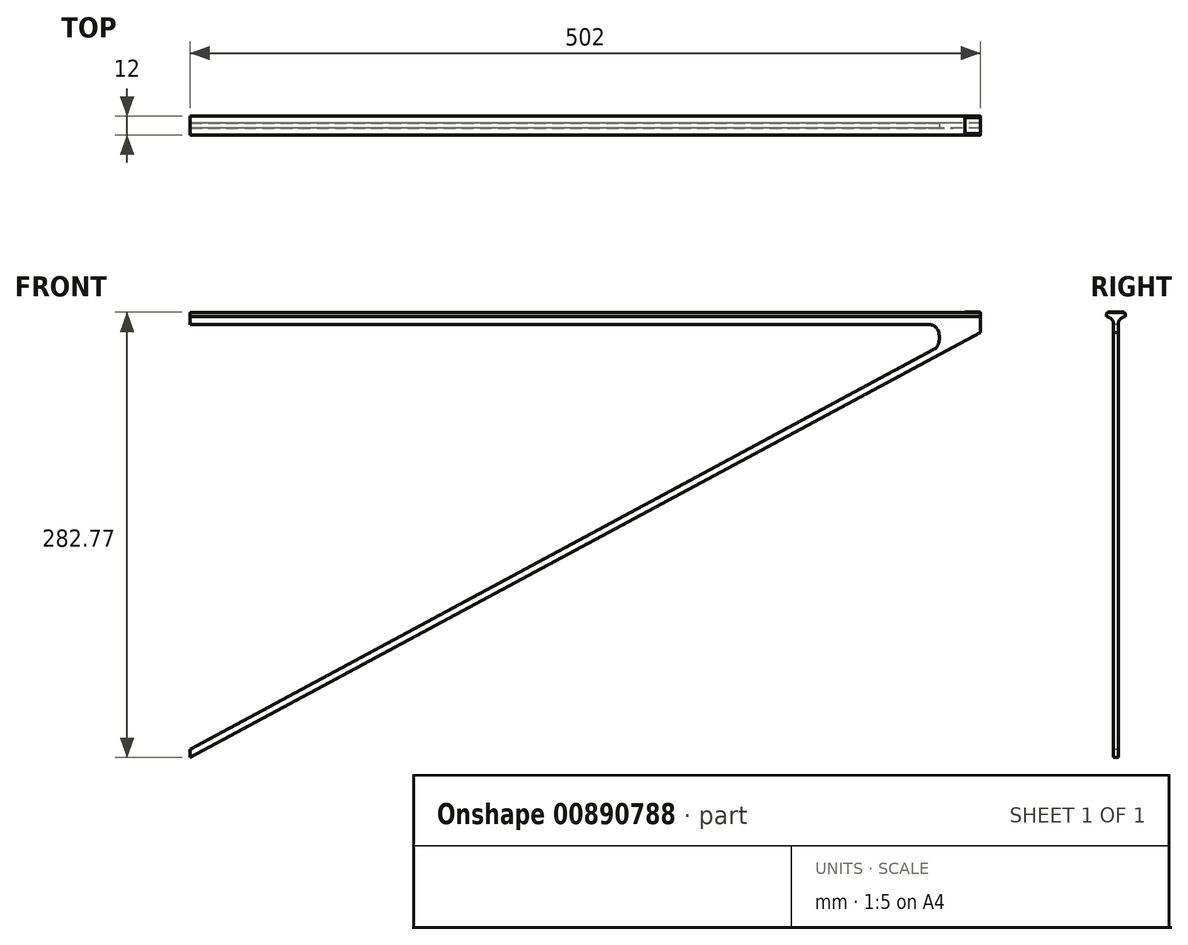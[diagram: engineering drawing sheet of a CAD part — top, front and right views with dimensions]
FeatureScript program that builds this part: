
annotation { "Feature Type Name" : "Feature", "Feature Type Description" : "" }
export const myFeature = defineFeature(function(context is Context, id is Id, definition is map)
    precondition{}
    {
        {
            var Q0;
            Q0=qCreatedBy(makeId("Right.planeOp"),FACE);
            var sketch = newSketch(context, id + "F0", { "sketchPlane" : qUnion([Q0])});
            skLineSegment(sketch, "E0", {"start": v(-6, 24.64) * mm, "end": v(6, 24.64) * mm});
            skLineSegment(sketch, "E1", {"start": v(-6, 24.64) * mm, "end": v(-6, 22.14) * mm});
            skLineSegment(sketch, "E2", {"start": v(-6, 22.14) * mm, "end": v(-1.5, 22.14) * mm});
            skLineSegment(sketch, "E3", {"start": v(-1.5, 22.14) * mm, "end": v(-1.5, -257.86) * mm});
            skLineSegment(sketch, "E4.MirrorCS", {"start": v(6, 22.14) * mm, "end": v(1.5, 22.14) * mm});
            skLineSegment(sketch, "E5.MirrorCS", {"start": v(6, 24.64) * mm, "end": v(6, 22.14) * mm});
            skLineSegment(sketch, "E6.MirrorCS", {"start": v(1.5, 22.14) * mm, "end": v(1.5, -257.86) * mm});
            skLineSegment(sketch, "E7", {"start": v(-1.5, -257.86) * mm, "end": v(1.5, -257.86) * mm});
            skSolve(sketch);
        }
        {
            var Q0;
            Q0=makeQuery(id+"F0.imprint","IMPRINT",FACE,{"disambiguationData":[TD([[makeQuery(id+"F0.imprint","IMPRINT",EDGE,{"derivedFrom":sQuery(id+"F0.wireOp",EDGE,"E0")}),-1.0]])]});
            extrude(context, id + "F1", {"entities" : qUnion([Q0]), "depth" : 502 * mm, "offsetDistance" : 25 * mm});
        }
        {
            var Q0;
            Q0=makeQuery(id+"F1.opExtrude","SWEPT_FACE",FACE,{"disambiguationData":[OSD([sQuery(id+"F0.wireOp",EDGE,"E3")])]});
            var sketch = newSketch(context, id + "F2", { "sketchPlane" : qUnion([Q0])});
            skPoint(sketch, "E8", {"position": v(502, 22.14) * mm});
            skPoint(sketch, "E9", {"position": v(502, 17.14) * mm});
            skPoint(sketch, "E10", {"position": v(0, -257.86) * mm});
            skPoint(sketch, "E11", {"position": v(0, -252.86) * mm});
            skLineSegment(sketch, "E12", {"start": v(502, 17.14) * mm, "end": v(0, 17.14) * mm});
            skLineSegment(sketch, "E13", {"start": v(502, 17.14) * mm, "end": v(0, -252.86) * mm});
            skPoint(sketch, "E14", {"position": v(502, 12.14) * mm});
            skLineSegment(sketch, "E15", {"start": v(0, -257.86) * mm, "end": v(502, 12.14) * mm});
            skSolve(sketch);
        }
        {
            var Q0;
            {var subQ0=sQuery(id+"F2.wireOp",EDGE,"E12");Q0=makeQuery(id+"F2.imprint","IMPRINT",FACE,{"disambiguationData":[TD([[makeQuery(id+"F2.imprint","IMPRINT",EDGE,{"derivedFrom":subQ0}),1.0]])]});}
            extrude(context, id + "F3", {"entities" : qUnion([Q0]), "operationType" : NewBodyOperationType.REMOVE, "oppositeDirection" : true, "depth" : 406 * mm, "offsetDistance" : 25 * mm});
        }
        {
            var Q0;
            {var subQ0=sQuery(id+"F2.wireOp",EDGE,"E15");Q0=makeQuery(id+"F2.imprint","IMPRINT",FACE,{"disambiguationData":[TD([[makeQuery(id+"F2.imprint","IMPRINT",EDGE,{"derivedFrom":subQ0}),-1.0]])]});}
            extrude(context, id + "F4", {"entities" : qUnion([Q0]), "operationType" : NewBodyOperationType.REMOVE, "oppositeDirection" : true, "depth" : 143 * mm, "offsetDistance" : 25 * mm});
        }
        {
            var Q0;
            Q0=makeQuery(id+"F3.boolean.opBoolean","COPY",FACE,{"derivedFrom":makeQuery(id+"F3.opExtrude","SWEPT_FACE",FACE,{"disambiguationData":[OSD([sQuery(id+"F2.wireOp",EDGE,"E12")])]})});
            var sketch = newSketch(context, id + "F5", { "sketchPlane" : qUnion([Q0])});
            skLineSegment(sketch, "E16.bottom", {"start": v(475.77, -1.5) * mm, "end": v(502, -1.5) * mm});
            skLineSegment(sketch, "E16.top", {"start": v(475.77, 1.5) * mm, "end": v(502, 1.5) * mm});
            skLineSegment(sketch, "E16.left", {"start": v(475.77, -1.5) * mm, "end": v(475.77, 1.5) * mm});
            skLineSegment(sketch, "E16.right", {"start": v(502, -1.5) * mm, "end": v(502, 1.5) * mm});
            skSolve(sketch);
        }
        {
            var Q0;
            Q0 = qSketchRegion(id + "F5", true);
            extrude(context, id + "F6", {"entities" : qUnion([Q0]), "operationType" : NewBodyOperationType.ADD, "depth" : 14.25 * mm, "offsetDistance" : 25 * mm, "hasSecondDirection" : true, "secondDirectionOppositeDirection" : true, "secondDirectionDepth" : 0.8 * mm});
        }
        {
            var Q0;
            {var subQ0=sQuery(id+"F0.wireOp",EDGE,"E7");var subQ1=sQuery(id+"F0.wireOp",EDGE,"E6.MirrorCS");var subQ3=sQuery(id+"F0.wireOp",EDGE,"E4.MirrorCS");var subQ10=makeQuery(id+"F1.opExtrude","SWEPT_FACE",FACE,{"disambiguationData":[OSD([subQ1])]});Q0=makeQuery(id+"F6.boolean.opBoolean","MERGE",FACE,{"derivedFrom":[makeQuery(id+"F3.boolean.opBoolean","SPLIT",FACE,{"disambiguationData":[TD([makeQuery(id+"F1.opExtrude","SWEPT_FACE",FACE,{"disambiguationData":[OSD([subQ3])]})])],"derivedFrom":subQ10}),makeQuery(id+"F3.boolean.opBoolean","SPLIT",FACE,{"disambiguationData":[TD([makeQuery(id+"F1.opExtrude","SWEPT_FACE",FACE,{"disambiguationData":[OSD([subQ0])]})])],"derivedFrom":subQ10}),makeQuery(id+"F6.opExtrude","SWEPT_FACE",FACE,{"disambiguationData":[OSD([sQuery(id+"F5.wireOp",EDGE,"E16.bottom")])]})]});}
            var sketch = newSketch(context, id + "F7", { "sketchPlane" : qUnion([Q0])});
            skLineSegment(sketch, "E17", {"start": v(-502, 12.14) * mm, "end": v(-484.8, 2.9) * mm});
            skLineSegment(sketch, "E18", {"start": v(-484.8, 2.9) * mm, "end": v(-502, 2.9) * mm});
            skLineSegment(sketch, "E19", {"start": v(-502, 2.9) * mm, "end": v(-502, 12.14) * mm});
            skSolve(sketch);
        }
        {
            var Q0;
            Q0=makeQuery(id+"F7.imprint","IMPRINT",FACE,{"disambiguationData":[TD([[makeQuery(id+"F7.imprint","IMPRINT",EDGE,{"derivedFrom":sQuery(id+"F7.wireOp",EDGE,"E17")}),-1.0]])]});
            extrude(context, id + "F8", {"entities" : qUnion([Q0]), "operationType" : NewBodyOperationType.REMOVE, "oppositeDirection" : true, "depth" : 25 * mm, "offsetDistance" : 25 * mm});
        }
        {
            var Q0;
            Q0=makeQuery(id+"F1.opExtrude","SWEPT_FACE",FACE,{"disambiguationData":[OSD([sQuery(id+"F0.wireOp",EDGE,"E0")])]});
            var sketch = newSketch(context, id + "F9", { "sketchPlane" : qUnion([Q0])});
            skLineSegment(sketch, "E20", {"start": v(496.5, -5.96) * mm, "end": v(496.5, -4.96) * mm});
            skLineSegment(sketch, "E21", {"start": v(497.84, 5.98) * mm, "end": v(497.84, 4.98) * mm});
            skLineSegment(sketch, "E22", {"start": v(501.98, 4.98) * mm, "end": v(491.98, 4.98) * mm});
            skLineSegment(sketch, "E23", {"start": v(491.98, 4.98) * mm, "end": v(491.98, -5.02) * mm});
            skLineSegment(sketch, "E24", {"start": v(491.98, -5.02) * mm, "end": v(501.98, -5.02) * mm});
            skLineSegment(sketch, "E25", {"start": v(501.98, -5.02) * mm, "end": v(501.98, 4.98) * mm});
            skSolve(sketch);
        }
        {
            var Q0;
            {var subQ6=sQuery(id+"F9.wireOp",EDGE,"oiYsljUy-fvYa-lGQO-kkHg-lW1iThUNzZ6y");Q0=makeQuery(id+"F9.imprint","IMPRINT",FACE,{"disambiguationData":[TD([[makeQuery(id+"F9.imprint","IMPRINT",EDGE,{"derivedFrom":subQ6}),1.0]])]});}
            var Q1;
            {var subQ1=sQuery(id+"F9.wireOp",EDGE,"E23");Q1=makeQuery(id+"F9.imprint","IMPRINT",FACE,{"disambiguationData":[TD([[makeQuery(id+"F9.imprint","IMPRINT",EDGE,{"derivedFrom":subQ1}),1.0]])]});}
            extrude(context, id + "F10", {"entities" : qUnion([Q0, Q1]), "operationType" : NewBodyOperationType.ADD, "depth" : 0.27 * mm, "offsetDistance" : 25 * mm});
        }
        {
            var Q0;
            Q0=makeQuery(id+"F6.boolean.opBoolean","INTERSECT",EDGE,{"derivedFrom":[makeQuery(id+"F3.boolean.opBoolean","COPY",FACE,{"derivedFrom":makeQuery(id+"F3.opExtrude","SWEPT_FACE",FACE,{"disambiguationData":[OSD([sQuery(id+"F2.wireOp",EDGE,"E12")])]})}),makeQuery(id+"F6.opExtrude","SWEPT_FACE",FACE,{"disambiguationData":[OSD([sQuery(id+"F5.wireOp",EDGE,"E16.left")])]})]});
            fillet(context, id + "F11", {"entities" : qUnion([Q0]), "radius" : 7 * mm, "tangentPropagation" : true, "allowEdgeOverflow" : false});
        }
        {
            var Q0;
            Q0=makeQuery(id+"F6.boolean.opBoolean","INTERSECT",EDGE,{"derivedFrom":[makeQuery(id+"F3.boolean.opBoolean","COPY",FACE,{"derivedFrom":makeQuery(id+"F3.opExtrude","SWEPT_FACE",FACE,{"disambiguationData":[OSD([sQuery(id+"F2.wireOp",EDGE,"E13")])]})}),makeQuery(id+"F6.opExtrude","SWEPT_FACE",FACE,{"disambiguationData":[OSD([sQuery(id+"F5.wireOp",EDGE,"E16.left")])]})]});
            fillet(context, id + "F12", {"entities" : qUnion([Q0]), "radius" : 7 * mm, "tangentPropagation" : true, "allowEdgeOverflow" : false});
        }
        {
            var Q0;
            Q0=makeQuery(id+"F1.opExtrude","SWEPT_EDGE",EDGE,{"disambiguationData":[OSD([sQuery(id+"F0.wireOp",EDGE,"E4.MirrorCS"),sQuery(id+"F0.wireOp",EDGE,"E6.MirrorCS")])]});
            fillet(context, id + "F13", {"entities" : qUnion([Q0]), "radius" : 5 * mm, "tangentPropagation" : true, "allowEdgeOverflow" : false});
        }
        {
            var Q0;
            Q0=makeQuery(id+"F1.opExtrude","SWEPT_EDGE",EDGE,{"disambiguationData":[OSD([sQuery(id+"F0.wireOp",EDGE,"E2"),sQuery(id+"F0.wireOp",EDGE,"E3")])]});
            fillet(context, id + "F14", {"entities" : qUnion([Q0]), "radius" : 5 * mm, "tangentPropagation" : true, "allowEdgeOverflow" : false});
        }
        {
            var Q0;
            Q0=makeQuery(id+"F1.opExtrude","SWEPT_EDGE",EDGE,{"disambiguationData":[OSD([sQuery(id+"F0.wireOp",EDGE,"E0"),sQuery(id+"F0.wireOp",EDGE,"E1")])]});
            var Q1;
            Q1=makeQuery(id+"F1.opExtrude","SWEPT_EDGE",EDGE,{"disambiguationData":[OSD([sQuery(id+"F0.wireOp",EDGE,"E0"),sQuery(id+"F0.wireOp",EDGE,"E5.MirrorCS")])]});
            fillet(context, id + "F15", {"entities" : qUnion([Q0, Q1]), "radius" : 1 * mm, "tangentPropagation" : true, "allowEdgeOverflow" : false});
        }
    });
